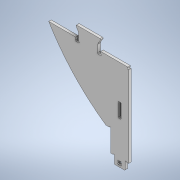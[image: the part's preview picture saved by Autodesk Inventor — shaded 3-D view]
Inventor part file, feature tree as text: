
AUTODESK INVENTOR PART (.ipt)
format: ipt  version: 2020 (Build 240168000, 168)  size: 276,480 bytes
history: native  units: mm
features: extrude x1, sketch x1
ambient origin geometry x8: Origin, YZ Plane, XZ Plane, XY Plane, X Axis, Y Axis, Z Axis, Center Point
bodies: Solid1 (feature_tree)
feature tree (2):
  extrude  "Extrusion1"  Depth=95.333333mm
  sketch  "Sketch1"  dims[d13=550.0mm d17=200.0mm d18=0.0mm d54=220.0mm d56=220.0mm d57=30.0mm d59=30.0mm d62=252.393783mm d73=236.680872mm d74=236.680872mm d75=576.435mm d76=472.393783mm d77=472.393783mm d78=30.0mm d81=220.0mm d82=252.393783mm d85=356.435mm d88=3.5mm d89=30.0mm d90=22.0mm d103=3.75mm d104=3.75mm d105=2.666667mm d106=30.0mm d107=20.0mm d108=2.666667mm d109=1.333333mm d110=7.333333mm d111=7.333333mm d112=7.5mm d113=3.75mm d114=3.75mm d134=3.5mm d135=65.0mm d136=65.0mm d137=7.333333mm d138=60.0deg d139=5.0mm d140=7.5mm d148=1.75mm d151=40.0mm d159=1.75mm d160=1.75mm d161=1.75mm d164=7.5mm d170=30.0mm d171=1.75mm d172=10.0mm d173=3.5mm d174=7.0mm d175=0.0mm d176=77.5mm d180=260.0mm d182=95.333333mm d184=230.666667mm d185=95.333333mm d186=97.083333mm d187=3.5mm]
